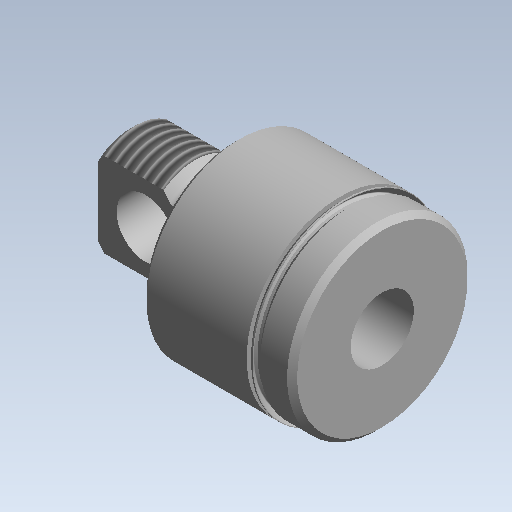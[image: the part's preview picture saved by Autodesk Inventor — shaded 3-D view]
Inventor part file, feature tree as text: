
AUTODESK INVENTOR PART (.ipt)
format: ipt  version: 2020 (Build 240168000, 168)  size: 304,128 bytes
history: native  units: mm (DEFAULTED — no unit token found)
features: other x168, sketch x7, revolve x4, thread x2, extrude x2, hole x1
ambient origin geometry x8: Origin, YZ Plane, XZ Plane, XY Plane, X Axis, Y Axis, Z Axis, Center Point
bodies: Solid1 (feature_tree)
feature tree (184):
  revolve  "Revolution1"  Angle=360.0deg
  revolve  "Revolution2"  [1 undecoded]
  thread  "Thread1"  [1 undecoded]
  extrude  "Extrusion1"  TaperAngle=360.0deg  [1 undecoded]
  hole  "Hole1"  [1 undecoded]
  revolve  "Revolution3"  [1 undecoded]
  thread  "Thread2"  [1 undecoded]
  revolve  "Revolution4"  [1 undecoded]
  extrude  "Extrusion2"  [1 undecoded]
  other  "1_XY"
  other  "1_YZ"
  other  "1_ZX"
  other  "1_X"
  other  "1_Y"
  other  "1_Z"
  other  "1_Center"
  other  "c1_XY"
  other  "c1_YZ"
  other  "c1_ZX"
  other  "c1_X"
  other  "c1_Y"
  other  "c1_Z"
  other  "c1_Center"
  other  "c2_XY"
  other  "c2_YZ"
  other  "c2_ZX"
  other  "c2_X"
  other  "c2_Y"
  other  "c2_Z"
  other  "c2_Center"
  other  "cc1_XY"
  other  "cc1_YZ"
  other  "cc1_ZX"
  other  "cc1_X"
  other  "cc1_Y"
  other  "cc1_Z"
  other  "cc1_Center"
  other  "cc2_XY"
  other  "cc2_YZ"
  other  "cc2_ZX"
  other  "cc2_X"
  other  "cc2_Y"
  other  "cc2_Z"
  other  "cc2_Center"
  other  "lovra1_XY"
  other  "lovra1_YZ"
  other  "lovra1_ZX"
  other  "lovra1_X"
  other  "lovra1_Y"
  other  "lovra1_Z"
  other  "lovra1_Center"
  other  "lovra2_XY"
  other  "lovra2_YZ"
  other  "lovra2_ZX"
  other  "lovra2_X"
  other  "lovra2_Y"
  other  "lovra2_Z"
  other  "lovra2_Center"
  other  "lovra21_XY"
  other  "lovra21_YZ"
  other  "lovra21_ZX"
  other  "lovra21_X"
  other  "lovra21_Y"
  other  "lovra21_Z"
  other  "lovra21_Center"
  other  "lovra22_XY"
  other  "lovra22_YZ"
  other  "lovra22_ZX"
  other  "lovra22_X"
  other  "lovra22_Y"
  other  "lovra22_Z"
  other  "lovra22_Center"
  other  "lovra3_XY"
  other  "lovra3_YZ"
  other  "lovra3_ZX"
  other  "lovra3_X"
  other  "lovra3_Y"
  other  "lovra3_Z"
  other  "lovra3_Center"
  other  "olen_XY"
  other  "olen_YZ"
  other  "olen_ZX"
  other  "olen_X"
  other  "olen_Y"
  other  "olen_Z"
  other  "olen_Center"
  other  "p1_XY"
  other  "p1_YZ"
  other  "p1_ZX"
  other  "p1_X"
  other  "p1_Y"
  other  "p1_Z"
  other  "p1_Center"
  other  "p2_XY"
  other  "p2_YZ"
  other  "p2_ZX"
  other  "p2_X"
  other  "p2_Y"
  other  "p2_Z"
  other  "p2_Center"
  other  "port_XY"
  other  "port_YZ"
  other  "port_ZX"
  other  "port_X"
  other  "port_Y"
  other  "port_Z"
  other  "port_Center"
  other  "port2_XY"
  other  "port2_YZ"
  other  "port2_ZX"
  other  "port2_X"
  other  "port2_Y"
  other  "port2_Z"
  other  "port2_Center"
  other  "thd1_XY"
  other  "thd1_YZ"
  other  "thd1_ZX"
  other  "thd1_X"
  other  "thd1_Y"
  other  "thd1_Z"
  other  "thd1_Center"
  other  "thd2_XY"
  other  "thd2_YZ"
  other  "thd2_ZX"
  other  "thd2_X"
  other  "thd2_Y"
  other  "thd2_Z"
  other  "thd2_Center"
  other  "to_mounting_bracket_XY"
  other  "to_mounting_bracket_YZ"
  other  "to_mounting_bracket_ZX"
  other  "to_mounting_bracket_X"
  other  "to_mounting_bracket_Y"
  other  "to_mounting_bracket_Z"
  other  "to_mounting_bracket_Center"
  other  "to_nut_XY"
  other  "to_nut_YZ"
  other  "to_nut_ZX"
  other  "to_nut_X"
  other  "to_nut_Y"
  other  "to_nut_Z"
  other  "to_nut_Center"
  other  "to_pin_XY"
  other  "to_pin_YZ"
  other  "to_pin_ZX"
  other  "to_pin_X"
  other  "to_pin_Y"
  other  "to_pin_Z"
  other  "to_pin_Center"
  other  "to_pin_1_XY"
  other  "to_pin_1_YZ"
  other  "to_pin_1_ZX"
  other  "to_pin_1_X"
  other  "to_pin_1_Y"
  other  "to_pin_1_Z"
  other  "to_pin_1_Center"
  other  "to_pin_r_XY"
  other  "to_pin_r_YZ"
  other  "to_pin_r_ZX"
  other  "to_pin_r_X"
  other  "to_pin_r_Y"
  other  "to_pin_r_Z"
  other  "to_pin_r_Center"
  other  "to_screw_XY"
  other  "to_screw_YZ"
  other  "to_screw_ZX"
  other  "to_screw_X"
  other  "to_screw_Y"
  other  "to_screw_Z"
  other  "to_screw_Center"
  other  "to_tube_XY"
  other  "to_tube_YZ"
  other  "to_tube_ZX"
  other  "to_tube_X"
  other  "to_tube_Y"
  other  "to_tube_Z"
  other  "to_tube_Center"
  sketch  "Sketch_18"  dims[d6=9.525mm d7=6.0mm d8=4.0mm d9=2.0mm d10=90.0deg d11=20.955mm d12=120.0deg d13=360.0deg]
  sketch  "Sketch_15"  dims[d2=9.00814mm d3=0.0mm d4=15.875mm d5=0.0mm]
  sketch  "Sketch_70"
  sketch  "Sketch4"  dims[d0=360.0deg d1=360.0deg]
  sketch  "Sketch_47"  dims[d19=0.0mm d20=0.0mm d21=0.0mm d22=0.0mm d23=0.0mm d24=0.0mm d25=0.0mm d26=0.0mm]
  sketch  "Sketch_24"  dims[d14=6.30226mm d15=0.0mm d16=360.0deg]
  sketch  "Sketch_43"  dims[d17=14.19225mm d18=0.0mm]
note: 8 required parameter values undecoded (feature->parameter linkage not recoverable at this tier; creation-order binding heuristic only, values carry confidence <= 0.55)